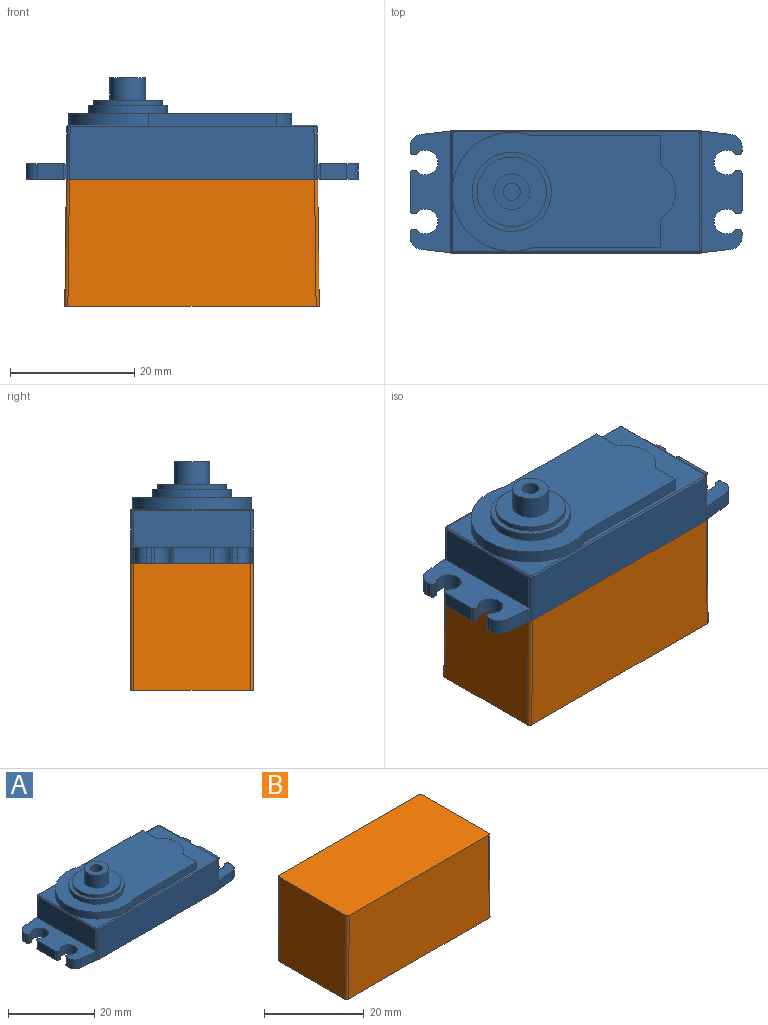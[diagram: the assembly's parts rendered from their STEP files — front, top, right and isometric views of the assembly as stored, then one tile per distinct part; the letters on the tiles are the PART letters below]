
ASSEMBLY  parts=2 mates=1
PART A: 83 faces, bbox 53.5x19.8x16.4 mm
  f0: plane 39.81x19.32mm, normal (0,0,1), area 173.8mm2, adj f54,f55,f56,f57,f58,f59,f73,f74
  f1: plane 18.8x5.95mm, normal (1,0,0.01), area 111.9mm2, adj f32,f69,f71,f79
  f2: plane 18.8x5.96mm, normal (-1,0,0.01), area 111.9mm2, adj f27,f70,f72,f74,f76,f78
  f3: plane 53.5x19.8mm, normal (0,0,-1), area 987.2mm2, adj f4,f5,f6,f7,f8,f9,f10,f11
  f4: plane 39.5x8.45mm, normal (0,-1,0), area 332.9mm2, adj f3,f71,f72,f75
  f5: plane 39.5x8.45mm, normal (0,1,0), area 332.9mm2, adj f3,f69,f70,f82
  f6: plane 4.28x2.5mm, normal (-0.11,-0.99,0), area 10.8mm2, adj f3,f7,f27,f28
  f7: cylinder r=2mm len=2.5mm, axis (0,0,-1), area 7.3mm2, adj f3,f6,f8,f27
  f8: plane 2.5x0.78mm, normal (-1,0,0), area 1.9mm2, adj f3,f7,f9,f27
  f9: cylinder r=0.5mm len=2.5mm, axis (0,0,-1), area 2mm2, adj f3,f8,f10,f27
  f10: plane 2.5x0.32mm, normal (0,1,0), area 0.8mm2, adj f3,f9,f11,f27
  f11: cylinder r=0.25mm len=2.5mm, axis (0,0,-1), area 0.5mm2, adj f3,f10,f12,f27
  f12: cylinder r=2mm len=4mm, axis (0,0,-1), area 24.1mm2, adj f3,f11,f13,f27
  f13: cylinder r=0.25mm len=2.5mm, axis (0,0,-1), area 0.5mm2, adj f3,f12,f14,f27
  f14: plane 2.5x0.32mm, normal (0,-1,0), area 0.8mm2, adj f3,f13,f15,f27
  f15: cylinder r=0.5mm len=2.5mm, axis (0,0,-1), area 2mm2, adj f3,f14,f16,f27
  f16: plane 6x2.5mm, normal (-1,0,0), area 15mm2, adj f3,f15,f17,f27
  f17: cylinder r=0.5mm len=2.5mm, axis (0,0,-1), area 2mm2, adj f3,f16,f18,f27
  f18: plane 2.5x0.32mm, normal (0,1,0), area 0.8mm2, adj f3,f17,f19,f27
  f19: cylinder r=0.25mm len=2.5mm, axis (0,0,-1), area 0.5mm2, adj f3,f18,f20,f27
  f20: cylinder r=2mm len=4mm, axis (0,0,-1), area 24.1mm2, adj f3,f19,f21,f27
  f21: cylinder r=0.25mm len=2.5mm, axis (0,0,-1), area 0.5mm2, adj f3,f20,f22,f27
  f22: plane 2.5x0.32mm, normal (0,-1,0), area 0.8mm2, adj f3,f21,f23,f27
  f23: cylinder r=0.5mm len=2.5mm, axis (0,0,-1), area 2mm2, adj f3,f22,f24,f27
  f24: plane 2.5x0.78mm, normal (-1,0,0), area 1.9mm2, adj f3,f23,f25,f27
  f25: cylinder r=2mm len=2.5mm, axis (0,0,-1), area 7.3mm2, adj f3,f24,f26,f27
  f26: plane 4.28x2.5mm, normal (-0.11,0.99,0), area 10.8mm2, adj f3,f25,f27,f29
  f27: plane 19.5x6.67mm, normal (0,0,1), area 93.3mm2, adj f2,f6,f7,f8,f9,f10,f11,f12
  f28: plane 2.5x0.62mm, normal (0,-1,0), area 1.5mm2, adj f3,f6,f27,f72
  f29: plane 2.5x0.62mm, normal (0,1,0), area 1.5mm2, adj f3,f26,f27,f70
  f30: plane 2.5x0.62mm, normal (0,1,0), area 1.5mm2, adj f3,f32,f49,f69
  f31: plane 2.5x0.62mm, normal (0,-1,0), area 1.5mm2, adj f3,f32,f50,f71
  f32: plane 19.5x6.67mm, normal (0,0,1), area 93.3mm2, adj f1,f30,f31,f33,f34,f35,f36,f37
  f33: plane 2.5x0.32mm, normal (0,1,0), area 0.8mm2, adj f3,f32,f34,f53
  f34: cylinder r=0.25mm len=2.5mm, axis (0,0,-1), area 0.5mm2, adj f3,f32,f33,f35
  f35: cylinder r=2mm len=4mm, axis (0,0,-1), area 24.1mm2, adj f3,f32,f34,f36
  f36: cylinder r=0.25mm len=2.5mm, axis (0,0,-1), area 0.5mm2, adj f3,f32,f35,f37
  f37: plane 2.5x0.32mm, normal (0,-1,0), area 0.8mm2, adj f3,f32,f36,f38
  f38: cylinder r=0.5mm len=2.5mm, axis (0,0,-1), area 2mm2, adj f3,f32,f37,f39
  f39: plane 6x2.5mm, normal (1,0,0), area 15mm2, adj f3,f32,f38,f40
  f40: cylinder r=0.5mm len=2.5mm, axis (0,0,-1), area 2mm2, adj f3,f32,f39,f41
  f41: plane 2.5x0.32mm, normal (0,1,0), area 0.8mm2, adj f3,f32,f40,f42
  f42: cylinder r=0.25mm len=2.5mm, axis (0,0,-1), area 0.5mm2, adj f3,f32,f41,f43
  f43: cylinder r=2mm len=4mm, axis (0,0,-1), area 24.1mm2, adj f3,f32,f42,f44
  f44: cylinder r=0.25mm len=2.5mm, axis (0,0,-1), area 0.5mm2, adj f3,f32,f43,f45
  f45: plane 2.5x0.32mm, normal (0,-1,0), area 0.8mm2, adj f3,f32,f44,f46
  f46: cylinder r=0.5mm len=2.5mm, axis (0,0,-1), area 2mm2, adj f3,f32,f45,f47
  f47: plane 2.5x0.78mm, normal (1,0,0), area 1.9mm2, adj f3,f32,f46,f48
  f48: cylinder r=2mm len=2.5mm, axis (0,0,-1), area 7.3mm2, adj f3,f32,f47,f49
  f49: plane 4.28x2.5mm, normal (0.11,0.99,0), area 10.8mm2, adj f3,f30,f32,f48
  f50: plane 4.28x2.5mm, normal (0.11,-0.99,0), area 10.8mm2, adj f3,f31,f32,f51
  f51: cylinder r=2mm len=2.5mm, axis (0,0,-1), area 7.3mm2, adj f3,f32,f50,f52
  f52: plane 2.5x0.78mm, normal (1,0,0), area 1.9mm2, adj f3,f32,f51,f53
  f53: cylinder r=0.5mm len=2.5mm, axis (0,0,-1), area 2mm2, adj f3,f32,f33,f52
  f54: plane 4.62x1.95mm, normal (1,0,0), area 9mm2, adj f0,f55,f59,f60
  f55: cylinder r=5.2mm len=8.76mm, axis (0,0,-1), area 20.3mm2, adj f0,f54,f56,f60
  f56: plane 4.62x1.95mm, normal (1,0,0), area 9mm2, adj f0,f55,f57,f60
  f57: plane 20.66x1.95mm, normal (0,1,0), area 40.3mm2, adj f0,f56,f58,f60
  f58: cylinder r=9.6mm len=19.2mm, axis (0,0,-1), area 72.1mm2, adj f0,f57,f59,f60,f76
  f59: plane 20.66x1.95mm, normal (0,-1,0), area 40.3mm2, adj f0,f54,f58,f60
  f60: plane 36x19.2mm, normal (0,0,1), area 465.6mm2, adj f54,f55,f56,f57,f58,f59,f61
  f61: cylinder r=6.4mm len=12.8mm, axis (0,0,-1), area 52.3mm2, adj f60,f62
  f62: plane 12.8x12.8mm, normal (0,0,1), area 30.2mm2, adj f61,f63
  f63: cylinder r=5.6mm len=11.2mm, axis (0,0,-1), area 28.1mm2, adj f62,f64
  f64: plane 11.2x11.2mm, normal (0,0,1), area 72.6mm2, adj f63,f65
  f65: cylinder r=2.88mm len=5.75mm, axis (0,0,-1), area 65.9mm2, adj f64,f66
  f66: plane 5.75x5.75mm, normal (0,0,1), area 20mm2, adj f65,f67
  f67: cylinder r=1.38mm len=5.75mm, axis (0,0,-1), area 49.7mm2, adj f66,f68
  f68: plane 2.75x2.75mm, normal (0,0,1), area 5.9mm2, adj f67
  f69: cylinder r=0.5mm len=8.46mm, axis (-0.01,0,1), area 5.7mm2, adj f1,f3,f5,f30,f32,f81
  f70: cylinder r=0.5mm len=8.46mm, axis (-0.01,0,-1), area 5.7mm2, adj f2,f3,f5,f27,f29,f80
  f71: cylinder r=0.5mm len=8.46mm, axis (0.01,0,-1), area 5.7mm2, adj f1,f3,f4,f31,f32,f77
  f72: cylinder r=0.5mm len=8.46mm, axis (0.01,0,1), area 5.7mm2, adj f2,f3,f4,f27,f28,f73
  f73: bspline ~0.5x0.5mm, area 0.3mm2, adj f0,f72,f74,f75
  f74: cylinder r=0.25mm len=8.39mm, axis (0,1,0), area 3.3mm2, adj f0,f2,f73,f76
  f75: cylinder r=0.25mm len=39.29mm, axis (1,0,0), area 15.4mm2, adj f0,f4,f73,f77
  f76: bspline ~2.02x0.25mm, area 0.7mm2, adj f2,f58,f74,f78
  f77: bspline ~0.5x0.5mm, area 0.3mm2, adj f0,f71,f75,f79
  f78: cylinder r=0.25mm len=8.39mm, axis (0,1,0), area 3.3mm2, adj f0,f2,f76,f80
  f79: cylinder r=0.25mm len=18.8mm, axis (0,1,0), area 7.3mm2, adj f0,f1,f77,f81
  f80: bspline ~0.5x0.5mm, area 0.3mm2, adj f0,f70,f78,f82
  f81: bspline ~0.5x0.5mm, area 0.3mm2, adj f0,f69,f79,f82
  f82: cylinder r=0.25mm len=39.29mm, axis (-1,0,0), area 15.4mm2, adj f0,f5,f80,f81
PART B: 10 faces, bbox 41x19.8x20.5 mm
  f0: plane 40.5x19.8mm, normal (0,0,1), area 801.7mm2, adj f1,f3,f4,f5,f6,f7,f8,f9
  f1: plane 20.5x18.8mm, normal (-1,0,0.01), area 385.4mm2, adj f0,f2,f6,f8
  f2: plane 41x19.8mm, normal (0,0,-1), area 811.6mm2, adj f1,f3,f4,f5,f6,f7,f8,f9
  f3: plane 20.5x18.8mm, normal (1,0,0.01), area 385.4mm2, adj f0,f2,f7,f9
  f4: plane 40x20.5mm, normal (0,-1,0), area 814.9mm2, adj f0,f2,f8,f9
  f5: plane 40x20.5mm, normal (0,1,0), area 814.9mm2, adj f0,f2,f6,f7
  f6: cylinder r=0.5mm len=20.51mm, axis (-0.01,0,-1), area 16.1mm2, adj f0,f1,f2,f5
  f7: cylinder r=0.5mm len=20.51mm, axis (-0.01,0,1), area 16.1mm2, adj f0,f2,f3,f5
  f8: cylinder r=0.5mm len=20.51mm, axis (0.01,0,1), area 16.1mm2, adj f0,f1,f2,f4
  f9: cylinder r=0.5mm len=20.51mm, axis (0.01,0,-1), area 16.1mm2, adj f0,f2,f3,f4
PLACE A at identity
PLACE B at identity fixed
MATE fastened B.f0 <-> A.f3  axis (0,0,1) through (0,0,0)mm
